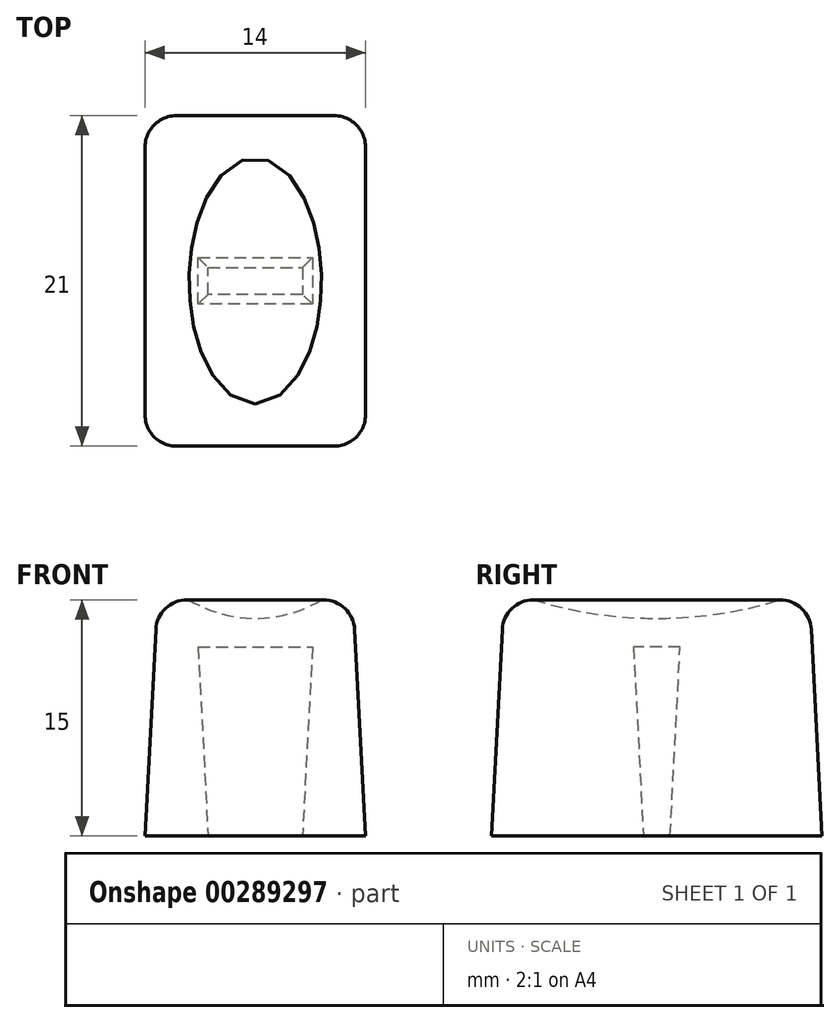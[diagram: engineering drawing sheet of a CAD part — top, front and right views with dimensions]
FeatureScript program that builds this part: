
annotation { "Feature Type Name" : "Feature", "Feature Type Description" : "" }
export const myFeature = defineFeature(function(context is Context, id is Id, definition is map)
    precondition{}
    {
        {
            var Q0;
            Q0=qCreatedBy(makeId("Top.planeOp"),FACE);
            var sketch = newSketch(context, id + "F0", { "sketchPlane" : qUnion([Q0])});
            skLineSegment(sketch, "E0.bottom", {"start": v(7, 10.5) * mm, "end": v(-7, 10.5) * mm});
            skLineSegment(sketch, "E0.top", {"start": v(7, -10.5) * mm, "end": v(-7, -10.5) * mm});
            skLineSegment(sketch, "E0.left", {"start": v(7, 10.5) * mm, "end": v(7, -10.5) * mm});
            skLineSegment(sketch, "E0.right", {"start": v(-7, 10.5) * mm, "end": v(-7, -10.5) * mm});
            skPoint(sketch, "E0.middle", {"position": v(0, 0) * mm});
            skLineSegment(sketch, "E1.bottom", {"start": v(3, 0.85) * mm, "end": v(-3, 0.85) * mm});
            skLineSegment(sketch, "E1.top", {"start": v(3, -0.85) * mm, "end": v(-3, -0.85) * mm});
            skLineSegment(sketch, "E1.left", {"start": v(3, 0.85) * mm, "end": v(3, -0.85) * mm});
            skLineSegment(sketch, "E1.right", {"start": v(-3, 0.85) * mm, "end": v(-3, -0.85) * mm});
            skSolve(sketch);
        }
        {
            var Q0;
            Q0=makeQuery(id+"F0.imprint","IMPRINT",FACE,{"disambiguationData":[TD([[makeQuery(id+"F0.imprint","IMPRINT",EDGE,{"derivedFrom":sQuery(id+"F0.wireOp",EDGE,"E0.bottom")}),1.0]])]});
            var Q1;
            Q1=makeQuery(id+"F0.imprint","IMPRINT",FACE,{"disambiguationData":[TD([[makeQuery(id+"F0.imprint","IMPRINT",EDGE,{"derivedFrom":sQuery(id+"F0.wireOp",EDGE,"E1.bottom")}),1.0]])]});
            extrude(context, id + "F1", {"entities" : qUnion([Q0, Q1]), "depth" : 15 * mm, "hasDraft" : true, "draftAngle" : 3 * degree, "draftPullDirection" : true});
        }
        {
            var Q0;
            Q0=makeQuery(id+"F0.imprint","IMPRINT",FACE,{"disambiguationData":[TD([[makeQuery(id+"F0.imprint","IMPRINT",EDGE,{"derivedFrom":sQuery(id+"F0.wireOp",EDGE,"E1.bottom")}),1.0]])]});
            extrude(context, id + "F2", {"entities" : qUnion([Q0]), "operationType" : NewBodyOperationType.REMOVE, "depth" : 12 * mm, "hasDraft" : true, "draftAngle" : 3 * degree});
        }
        {
            var Q0;
            Q0=makeQuery(id+"F1.opExtrude","SWEPT_EDGE",EDGE,{"disambiguationData":[OSD([sQuery(id+"F0.wireOp",EDGE,"E0.bottom"),sQuery(id+"F0.wireOp",EDGE,"E0.right")])]});
            var Q1;
            Q1=makeQuery(id+"F1.opExtrude","SWEPT_EDGE",EDGE,{"disambiguationData":[OSD([sQuery(id+"F0.wireOp",EDGE,"E0.top"),sQuery(id+"F0.wireOp",EDGE,"E0.right")])]});
            var Q2;
            Q2=makeQuery(id+"F1.opExtrude","SWEPT_EDGE",EDGE,{"disambiguationData":[OSD([sQuery(id+"F0.wireOp",EDGE,"E0.bottom"),sQuery(id+"F0.wireOp",EDGE,"E0.left")])]});
            var Q3;
            Q3=makeQuery(id+"F1.opExtrude","SWEPT_EDGE",EDGE,{"disambiguationData":[OSD([sQuery(id+"F0.wireOp",EDGE,"E0.top"),sQuery(id+"F0.wireOp",EDGE,"E0.left")])]});
            var Q4;
            Q4=makeQuery(id+"F1.opExtrude","CAP_EDGE",EDGE,{"disambiguationData":[OSD([sQuery(id+"F0.wireOp",EDGE,"E0.left")])],"isStart":false});
            var Q5;
            Q5=makeQuery(id+"F1.opExtrude","CAP_EDGE",EDGE,{"disambiguationData":[OSD([sQuery(id+"F0.wireOp",EDGE,"E0.top")])],"isStart":false});
            var Q6;
            Q6=makeQuery(id+"F1.opExtrude","CAP_FACE",FACE,{"disambiguationData":[OSD([sQuery(id+"F0.wireOp",EDGE,"E0.bottom"),sQuery(id+"F0.wireOp",EDGE,"E0.top"),sQuery(id+"F0.wireOp",EDGE,"E0.left"),sQuery(id+"F0.wireOp",EDGE,"E0.right")])],"isStart":false});
            fillet(context, id + "F3", {"entities" : qUnion([Q0, Q1, Q2, Q3, Q4, Q5, Q6]), "radius" : 2 * mm, "tangentPropagation" : true, "allowEdgeOverflow" : false});
        }
        {
            var Q0;
            Q0=qCreatedBy(makeId("Top.planeOp"),FACE);
            var sketch = newSketch(context, id + "F4", { "sketchPlane" : qUnion([Q0])});
            skEllipticalArc(sketch, "E2", {});
            skLineSegment(sketch, "E3", {"start": v(0, 13.58) * mm, "end": v(0, -14.41) * mm, "construction": true});
            skLineSegment(sketch, "E4", {"start": v(0, -15) * mm, "end": v(0, 15) * mm});
            const initialGuessF4  = {"E2": [0, 0, 0, 1, 0.015, 0.008083219246524585, 3.141592653589793, 0]};
            skSetInitialGuess(sketch, initialGuessF4);
            skSolve(sketch);
        }
        {
            var Q0;
            Q0=makeQuery(id+"F4.imprint","IMPRINT",FACE,{"disambiguationData":[TD([[makeQuery(id+"F4.imprint","IMPRINT",EDGE,{"derivedFrom":sQuery(id+"F4.wireOp",EDGE,"E2")}),1.0]])]});
            var Q1;
            Q1=sQuery(id+"F4.wireOp",EDGE,"E3");
            revolve(context, id + "F5", {"entities" : qUnion([Q0]), "axis" : qUnion([Q1]), "revolveType" : RevolveType.FULL});
        }
        {
            var Q0;
            Q0=makeQuery(id+"F5.opRevolve","SWEPT_BODY",BODY,{"disambiguationData":[OSD([sQuery(id+"F4.wireOp",EDGE,"E2"),sQuery(id+"F4.wireOp",EDGE,"E4")])]});
            transform(context, id + "F6", {"entities" : qUnion([Q0]), "transformType" : TransformType.TRANSLATION_3D, "dx" : 0 * mm, "dy" : 0 * mm, "dz" : 21.9 * mm, "makeCopy" : false});
        }
        {
            var Q0;
            Q0=makeQuery(id+"F5.opRevolve","SWEPT_BODY",BODY,{"disambiguationData":[OSD([sQuery(id+"F4.wireOp",EDGE,"E2"),sQuery(id+"F4.wireOp",EDGE,"E4")])]});
            var Q1;
            Q1=makeQuery(id+"F1.opExtrude","SWEPT_BODY",BODY,{"disambiguationData":[OSD([sQuery(id+"F0.wireOp",EDGE,"E0.bottom"),sQuery(id+"F0.wireOp",EDGE,"E0.top"),sQuery(id+"F0.wireOp",EDGE,"E0.left"),sQuery(id+"F0.wireOp",EDGE,"E0.right")])]});
            booleanBodies(context, id + "F7", {"operationType" : BooleanOperationType.SUBTRACTION, "tools" : qUnion([Q0]), "targets" : qUnion([Q1])});
        }
    });
